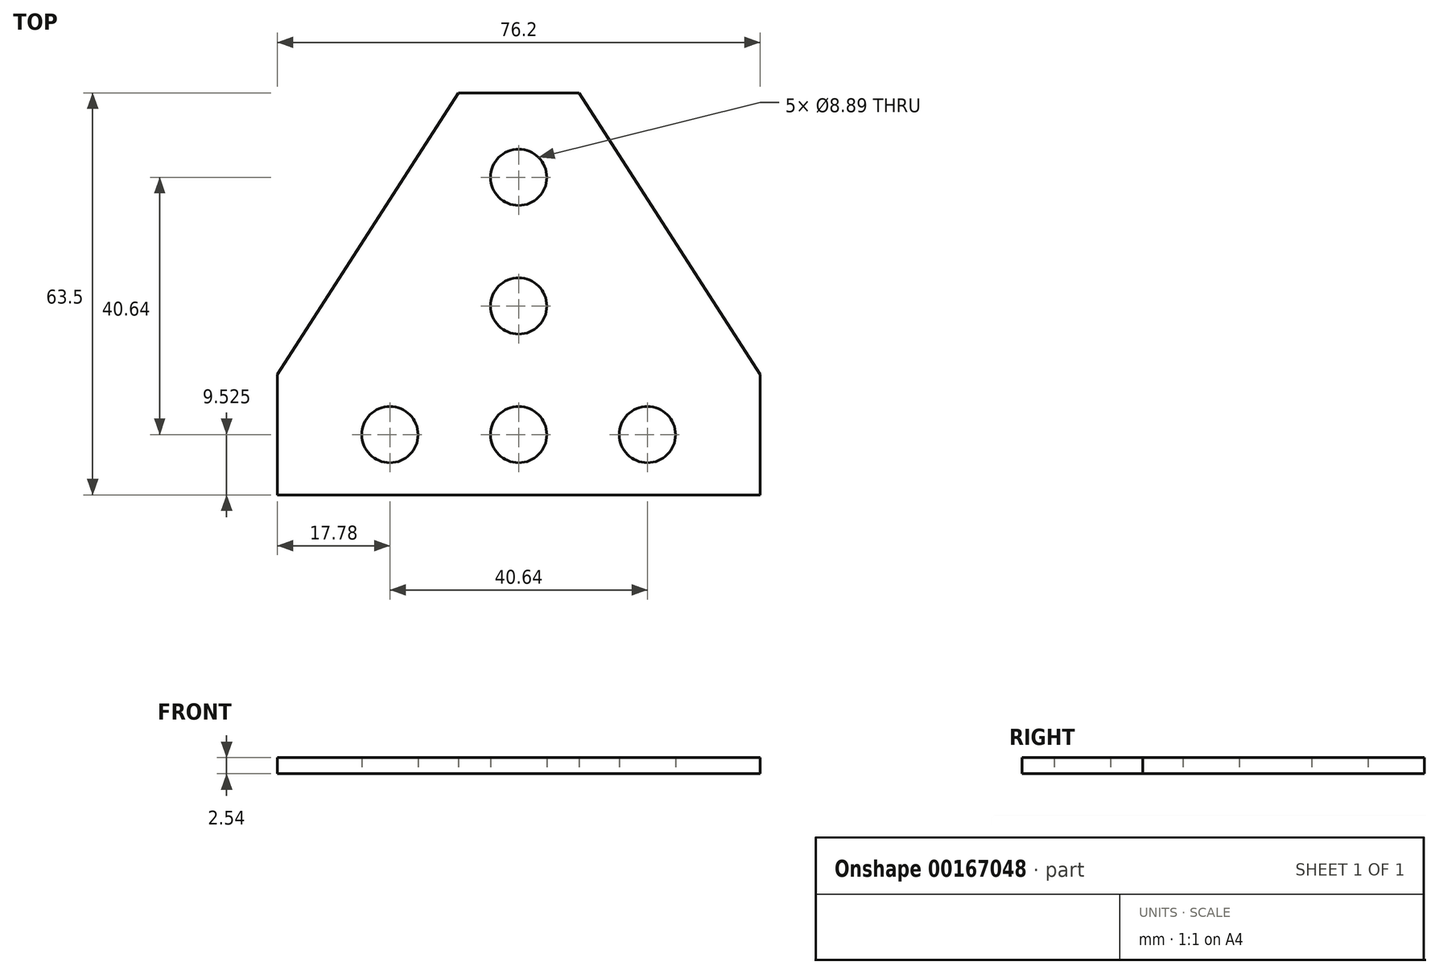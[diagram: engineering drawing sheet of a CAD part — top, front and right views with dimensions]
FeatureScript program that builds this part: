
annotation { "Feature Type Name" : "Feature", "Feature Type Description" : "" }
export const myFeature = defineFeature(function(context is Context, id is Id, definition is map)
    precondition{}
    {
        {
            var Q0;
            Q0=qCreatedBy(makeId("Top.planeOp"),FACE);
            var sketch = newSketch(context, id + "F0", { "sketchPlane" : qUnion([Q0])});
            skLineSegment(sketch, "E0.bottom", {"start": v(0, 0) * mm, "end": v(-76.2, 0) * mm});
            skLineSegment(sketch, "E0.top", {"start": v(0, 19.05) * mm, "end": v(-76.2, 19.05) * mm, "construction": true});
            skLineSegment(sketch, "E0.left", {"start": v(0, 0) * mm, "end": v(0, 19.05) * mm});
            skLineSegment(sketch, "E0.right", {"start": v(-76.2, 0) * mm, "end": v(-76.2, 19.05) * mm});
            skLineSegment(sketch, "E1", {"start": v(-76.2, 19.05) * mm, "end": v(-47.63, 63.5) * mm});
            skLineSegment(sketch, "E2", {"start": v(-47.63, 63.5) * mm, "end": v(-28.57, 63.5) * mm});
            skLineSegment(sketch, "E3", {"start": v(-28.57, 63.5) * mm, "end": v(0, 19.05) * mm});
            skCircle(sketch, "E4", {"center": v(-38.1, 50.17) * mm, "radius": 4.45 * mm});
            skCircle(sketch, "E5", {"center": v(-38.1, 29.85) * mm, "radius": 4.45 * mm});
            skCircle(sketch, "E6", {"center": v(-38.1, 9.53) * mm, "radius": 4.45 * mm});
            skCircle(sketch, "E7", {"center": v(-17.78, 9.52) * mm, "radius": 4.45 * mm});
            skCircle(sketch, "E8", {"center": v(-58.42, 9.52) * mm, "radius": 4.45 * mm});
            skLineSegment(sketch, "E9", {"start": v(-76.2, 9.53) * mm, "end": v(0, 9.53) * mm, "construction": true});
            skLineSegment(sketch, "E10", {"start": v(-38.1, 63.5) * mm, "end": v(-38.1, 0) * mm, "construction": true});
            skLineSegment(sketch, "E11", {"start": v(-38.1, 50.17) * mm, "end": v(-38.1, 29.85) * mm, "construction": true});
            skSolve(sketch);
        }
        {
            var Q0;
            Q0 = qSketchRegion(id + "F0", true);
            extrude(context, id + "F1", {"entities" : qUnion([Q0]), "depth" : 2.54 * mm});
        }
    });
